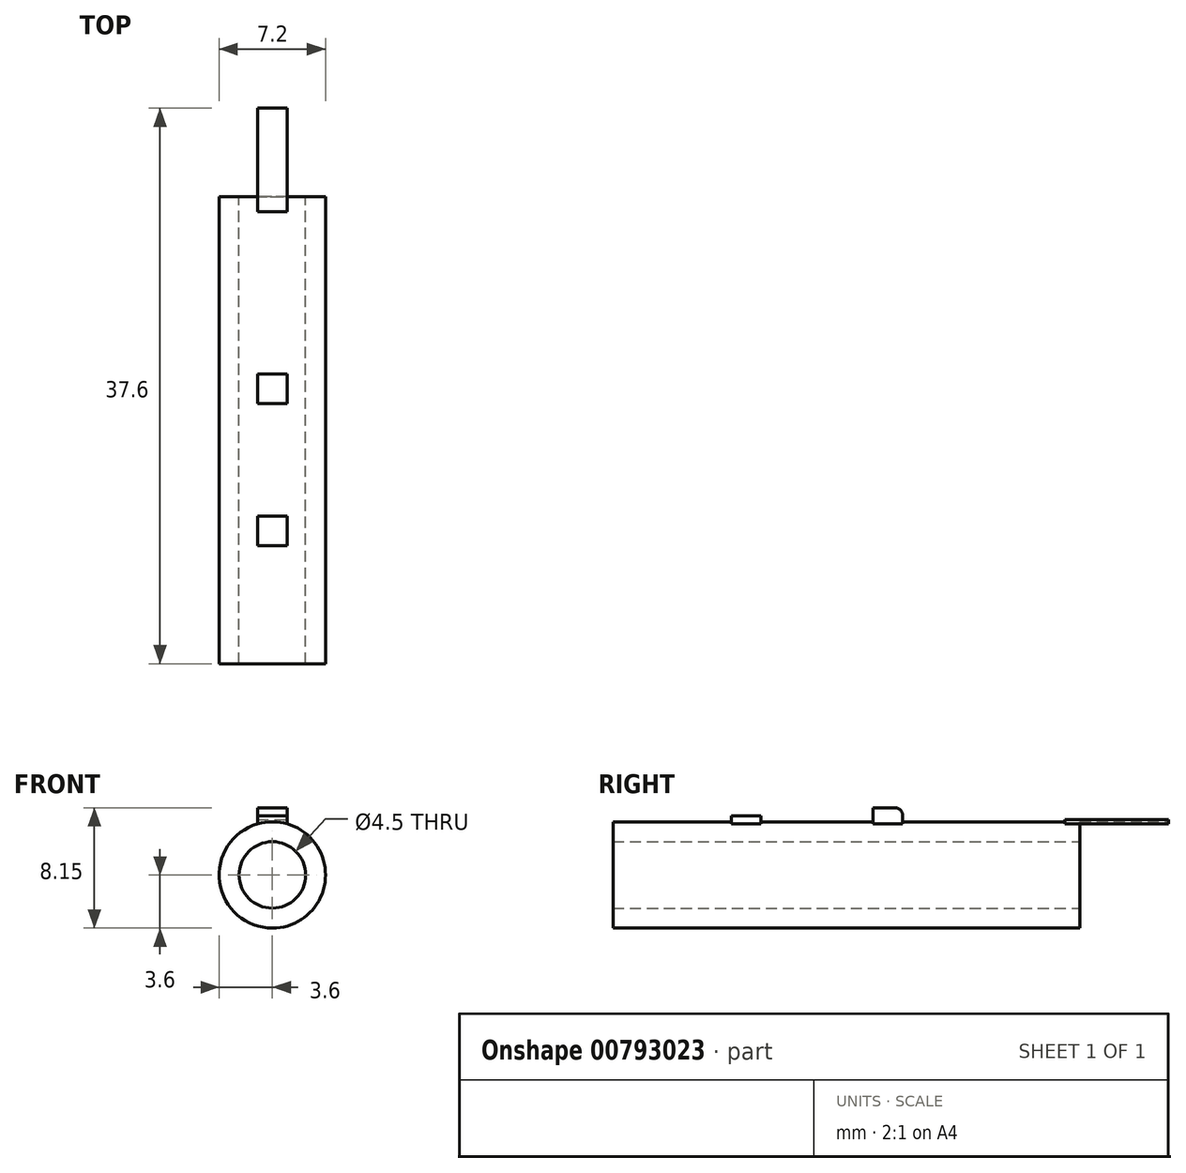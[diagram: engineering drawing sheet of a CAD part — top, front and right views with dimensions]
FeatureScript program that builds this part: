
annotation { "Feature Type Name" : "Feature", "Feature Type Description" : "" }
export const myFeature = defineFeature(function(context is Context, id is Id, definition is map)
    precondition{}
    {
        {
            var Q0;
            Q0=qCreatedBy(makeId("Front.planeOp"),FACE);
            var sketch = newSketch(context, id + "F0", { "sketchPlane" : qUnion([Q0])});
            skCircle(sketch, "E0", {"center": v(0, 0) * mm, "radius": 2.25 * mm});
            skCircle(sketch, "E1", {"center": v(0, 0) * mm, "radius": 3.6 * mm});
            skSolve(sketch);
        }
        {
            var Q0;
            Q0 = qSketchRegion(id + "F0", true);
            extrude(context, id + "F1", {"entities" : qUnion([Q0]), "depth" : 37.6 * mm, "offsetDistance" : 25 * mm, "symmetric" : true});
        }
        {
            var Q0;
            Q0=makeQuery(id+"F1.opExtrude","CAP_FACE",FACE,{"disambiguationData":[OSD([sQuery(id+"F0.wireOp",EDGE,"E0"),sQuery(id+"F0.wireOp",EDGE,"E1")])],"isStart":false});
            var sketch = newSketch(context, id + "F2", { "sketchPlane" : qUnion([Q0])});
            skLineSegment(sketch, "E2.top", {"start": v(1, 4.55) * mm, "end": v(-1, 4.55) * mm});
            skLineSegment(sketch, "E2.left", {"start": v(1, 3.46) * mm, "end": v(1, 4.55) * mm});
            skLineSegment(sketch, "E2.right", {"start": v(-1, 3.46) * mm, "end": v(-1, 4.55) * mm});
            skPoint(sketch, "E2.middle", {"position": v(0, 3.6) * mm});
            skPoint(sketch, "E3", {"position": v(-1, 3.46) * mm});
            skPoint(sketch, "E4", {"position": v(1, 3.46) * mm});
            skLineSegment(sketch, "E5", {"start": v(0, 4.55) * mm, "end": v(0, 3.6) * mm, "construction": true});
            skSolve(sketch);
        }
        {
            var Q0;
            Q0=makeQuery(id+"F2.imprint","IMPRINT",FACE,{"disambiguationData":[TD([[makeQuery(id+"F2.imprint","IMPRINT",EDGE,{"derivedFrom":sQuery(id+"F2.wireOp",EDGE,"E2.top")}),1.0]])]});
            extrude(context, id + "F3", {"entities" : qUnion([Q0]), "operationType" : NewBodyOperationType.ADD, "oppositeDirection" : true, "depth" : 19.6 * mm, "offsetDistance" : 25 * mm});
        }
        {
            var Q0;
            {var subQ0=sQuery(id+"F0.wireOp",EDGE,"E1");Q0=makeQuery(id+"F3.boolean.opBoolean","MERGE",FACE,{"derivedFrom":[makeQuery(id+"F1.opExtrude","CAP_FACE",FACE,{"disambiguationData":[OSD([sQuery(id+"F0.wireOp",EDGE,"E0"),subQ0])],"isStart":false}),makeQuery(id+"F3.opExtrude","CAP_FACE",FACE,{"disambiguationData":[OSD([subQ0,sQuery(id+"F2.wireOp",EDGE,"E2.top"),sQuery(id+"F2.wireOp",EDGE,"E2.left"),sQuery(id+"F2.wireOp",EDGE,"E2.right")])],"isStart":true})]});}
            var sketch = newSketch(context, id + "F4", { "sketchPlane" : qUnion([Q0])});
            skCircle(sketch, "E6", {"center": v(0, 0) * mm, "radius": 3.6 * mm});
            skSolve(sketch);
        }
        {
            var Q0;
            Q0=makeQuery(id+"F4.imprint","IMPRINT",FACE,{"disambiguationData":[TD([[makeQuery(id+"F4.imprint","IMPRINT",EDGE,{"derivedFrom":makeQuery(id+"F3.opExtrude","CAP_EDGE",EDGE,{"disambiguationData":[OSD([sQuery(id+"F2.wireOp",EDGE,"E2.top")])],"isStart":true})}),1.0]])]});
            extrude(context, id + "F5", {"entities" : qUnion([Q0]), "operationType" : NewBodyOperationType.REMOVE, "oppositeDirection" : true, "depth" : 17.6 * mm, "offsetDistance" : 25 * mm});
        }
        {
            var Q0;
            {var subQ0=sQuery(id+"F0.wireOp",EDGE,"E1");Q0=makeQuery(id+"F3.boolean.opBoolean","MERGE",FACE,{"derivedFrom":[makeQuery(id+"F1.opExtrude","CAP_FACE",FACE,{"disambiguationData":[OSD([sQuery(id+"F0.wireOp",EDGE,"E0"),subQ0])],"isStart":false}),makeQuery(id+"F3.opExtrude","CAP_FACE",FACE,{"disambiguationData":[OSD([subQ0,sQuery(id+"F2.wireOp",EDGE,"E2.top"),sQuery(id+"F2.wireOp",EDGE,"E2.left"),sQuery(id+"F2.wireOp",EDGE,"E2.right")])],"isStart":true})]});}
            var sketch = newSketch(context, id + "F6", { "sketchPlane" : qUnion([Q0])});
            skCircle(sketch, "E7", {"center": v(0, 0) * mm, "radius": 3.6 * mm});
            skLineSegment(sketch, "E8.top", {"start": v(1, 4) * mm, "end": v(-1, 4) * mm});
            skLineSegment(sketch, "E8.left", {"start": v(1, 3.46) * mm, "end": v(1, 4) * mm});
            skLineSegment(sketch, "E8.right", {"start": v(-1, 3.46) * mm, "end": v(-1, 4) * mm});
            skPoint(sketch, "E8.middle", {"position": v(0, 3.6) * mm});
            skPoint(sketch, "E9", {"position": v(-1, 3.46) * mm});
            skPoint(sketch, "E10", {"position": v(1, 3.46) * mm});
            skSolve(sketch);
        }
        {
            var Q0;
            Q0=makeQuery(id+"F6.imprint","IMPRINT",FACE,{"disambiguationData":[TD([[makeQuery(id+"F6.imprint","IMPRINT",EDGE,{"derivedFrom":sQuery(id+"F6.wireOp",EDGE,"E8.top")}),1.0]])]});
            extrude(context, id + "F7", {"entities" : qUnion([Q0]), "operationType" : NewBodyOperationType.ADD, "oppositeDirection" : true, "depth" : 10 * mm, "offsetDistance" : 25 * mm});
        }
        {
            var Q0;
            {var subQ0=sQuery(id+"F0.wireOp",EDGE,"E1");Q0=makeQuery(id+"F7.boolean.opBoolean","MERGE",FACE,{"derivedFrom":[makeQuery(id+"F3.boolean.opBoolean","MERGE",FACE,{"derivedFrom":[makeQuery(id+"F1.opExtrude","CAP_FACE",FACE,{"disambiguationData":[OSD([sQuery(id+"F0.wireOp",EDGE,"E0"),subQ0])],"isStart":false}),makeQuery(id+"F3.opExtrude","CAP_FACE",FACE,{"disambiguationData":[OSD([subQ0,sQuery(id+"F2.wireOp",EDGE,"E2.top"),sQuery(id+"F2.wireOp",EDGE,"E2.left"),sQuery(id+"F2.wireOp",EDGE,"E2.right")])],"isStart":true})]}),makeQuery(id+"F7.opExtrude","CAP_FACE",FACE,{"disambiguationData":[OSD([sQuery(id+"F6.wireOp",EDGE,"E7"),sQuery(id+"F6.wireOp",EDGE,"E8.top"),sQuery(id+"F6.wireOp",EDGE,"E8.left"),sQuery(id+"F6.wireOp",EDGE,"E8.right")])],"isStart":true})]});}
            var sketch = newSketch(context, id + "F8", { "sketchPlane" : qUnion([Q0])});
            skCircle(sketch, "E11", {"center": v(0, 0) * mm, "radius": 3.6 * mm});
            skSolve(sketch);
        }
        {
            var Q0;
            Q0=makeQuery(id+"F8.imprint","IMPRINT",FACE,{"disambiguationData":[TD([[makeQuery(id+"F8.imprint","IMPRINT",EDGE,{"derivedFrom":makeQuery(id+"F7.opExtrude","CAP_EDGE",EDGE,{"disambiguationData":[OSD([sQuery(id+"F6.wireOp",EDGE,"E8.top")])],"isStart":true})}),1.0]])]});
            extrude(context, id + "F9", {"entities" : qUnion([Q0]), "operationType" : NewBodyOperationType.REMOVE, "oppositeDirection" : true, "depth" : 8 * mm, "offsetDistance" : 25 * mm});
        }
        {
            var Q0;
            Q0=makeQuery(id+"F1.opExtrude","CAP_FACE",FACE,{"disambiguationData":[OSD([sQuery(id+"F0.wireOp",EDGE,"E0"),sQuery(id+"F0.wireOp",EDGE,"E1")])],"isStart":true});
            var sketch = newSketch(context, id + "F10", { "sketchPlane" : qUnion([Q0])});
            skLineSegment(sketch, "E12.top", {"start": v(1, 3.74) * mm, "end": v(-1, 3.74) * mm});
            skLineSegment(sketch, "E12.left", {"start": v(1, 3.46) * mm, "end": v(1, 3.74) * mm});
            skLineSegment(sketch, "E12.right", {"start": v(-1, 3.46) * mm, "end": v(-1, 3.74) * mm});
            skPoint(sketch, "E12.middle", {"position": v(0, 3.6) * mm});
            skSolve(sketch);
        }
        {
            var Q0;
            Q0=makeQuery(id+"F10.imprint","IMPRINT",FACE,{"disambiguationData":[TD([[makeQuery(id+"F10.imprint","IMPRINT",EDGE,{"derivedFrom":sQuery(id+"F10.wireOp",EDGE,"E12.top")}),1.0]])]});
            extrude(context, id + "F11", {"entities" : qUnion([Q0]), "operationType" : NewBodyOperationType.ADD, "oppositeDirection" : true, "depth" : 7 * mm, "offsetDistance" : 25 * mm});
        }
        {
            var Q0;
            {var subQ0=sQuery(id+"F0.wireOp",EDGE,"E1");Q0=makeQuery(id+"F11.boolean.opBoolean","MERGE",FACE,{"derivedFrom":[makeQuery(id+"F1.opExtrude","CAP_FACE",FACE,{"disambiguationData":[OSD([sQuery(id+"F0.wireOp",EDGE,"E0"),subQ0])],"isStart":true}),makeQuery(id+"F11.opExtrude","CAP_FACE",FACE,{"disambiguationData":[OSD([subQ0,sQuery(id+"F10.wireOp",EDGE,"E12.top"),sQuery(id+"F10.wireOp",EDGE,"E12.left"),sQuery(id+"F10.wireOp",EDGE,"E12.right")])],"isStart":true})]});}
            var sketch = newSketch(context, id + "F12", { "sketchPlane" : qUnion([Q0])});
            skCircle(sketch, "E13", {"center": v(0, 0) * mm, "radius": 3.6 * mm});
            skSolve(sketch);
        }
        {
            var Q0;
            Q0=makeQuery(id+"F12.imprint","IMPRINT",FACE,{"disambiguationData":[TD([[makeQuery(id+"F12.imprint","IMPRINT",EDGE,{"disambiguationData":[OD(0.0)],"derivedFrom":sQuery(id+"F12.wireOp",EDGE,"E13")}),-1.0]])]});
            extrude(context, id + "F13", {"entities" : qUnion([Q0]), "operationType" : NewBodyOperationType.REMOVE, "oppositeDirection" : true, "depth" : 6 * mm, "offsetDistance" : 25 * mm});
        }
        {
            var Q0;
            Q0=makeQuery(id+"F3.opExtrude","CAP_EDGE",EDGE,{"disambiguationData":[OSD([sQuery(id+"F2.wireOp",EDGE,"E2.top")])],"isStart":false});
            var Q1;
            Q1=makeQuery(id+"F5.boolean.opBoolean","COPY",EDGE,{"derivedFrom":makeQuery(id+"F5.opExtrude","CAP_EDGE",EDGE,{"disambiguationData":[OSD([sQuery(id+"F2.wireOp",EDGE,"E2.top")])],"isStart":false})});
            fillet(context, id + "F14", {"entities" : qUnion([Q0, Q1]), "radius" : 0.5 * mm, "tangentPropagation" : true, "allowEdgeOverflow" : false});
        }
    });
